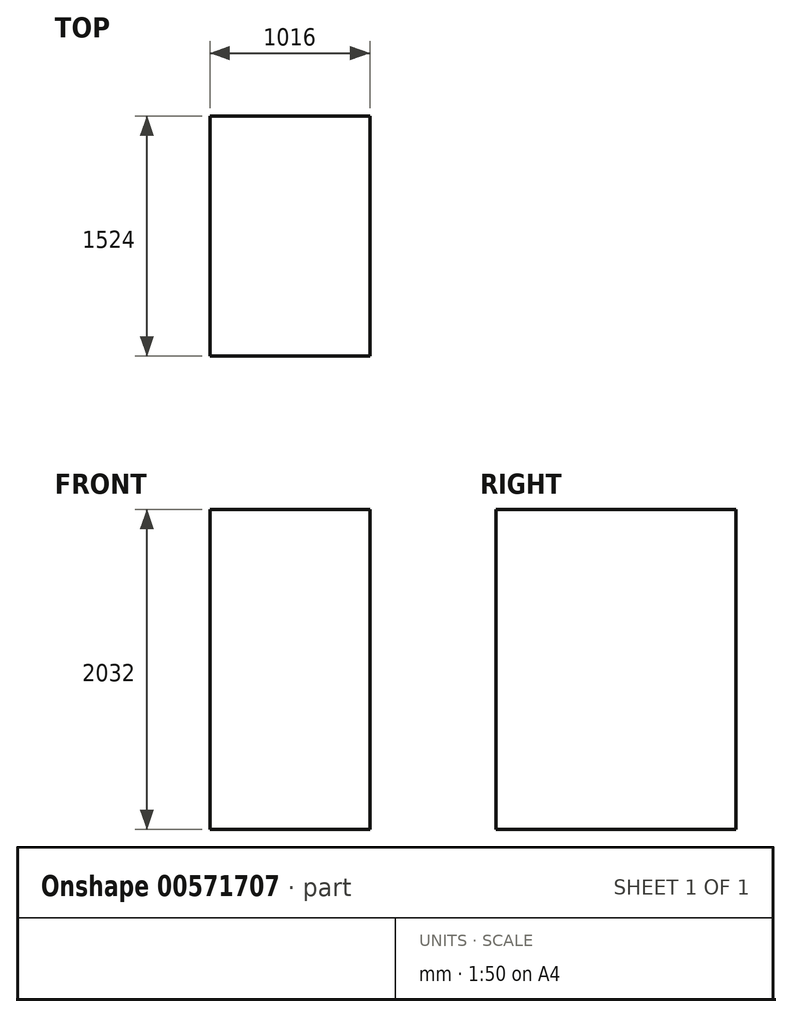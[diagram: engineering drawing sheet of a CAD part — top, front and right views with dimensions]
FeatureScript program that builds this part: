
annotation { "Feature Type Name" : "Feature", "Feature Type Description" : "" }
export const myFeature = defineFeature(function(context is Context, id is Id, definition is map)
    precondition{}
    {
        {
            var Q0;
            Q0=qCreatedBy(makeId("Top.planeOp"),FACE);
            var sketch = newSketch(context, id + "F0", { "sketchPlane" : qUnion([Q0])});
            skLineSegment(sketch, "E0.bottom", {"start": v(0, 0) * mm, "end": v(1016, 0) * mm});
            skLineSegment(sketch, "E0.top", {"start": v(0, 1524) * mm, "end": v(1016, 1524) * mm});
            skLineSegment(sketch, "E0.left", {"start": v(0, 0) * mm, "end": v(0, 1524) * mm});
            skLineSegment(sketch, "E0.right", {"start": v(1016, 0) * mm, "end": v(1016, 1524) * mm});
            skSolve(sketch);
        }
        {
            var Q0;
            Q0 = qSketchRegion(id + "F0", true);
            extrude(context, id + "F1", {"entities" : qUnion([Q0]), "depth" : 2032 * mm, "offsetDistance" : 25.4 * mm});
        }
    });
